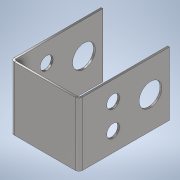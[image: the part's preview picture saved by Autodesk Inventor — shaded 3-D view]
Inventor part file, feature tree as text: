
AUTODESK INVENTOR PART (.ipt)
format: ipt  version: 2022 (Build 260153000, 153)  size: 192,512 bytes
history: native  units: mm
features: sheet_metal_op x3, sketch x2, other x2, extrude x1, projected_geometry x1
ambient origin geometry x8: Origin, YZ Plane, XZ Plane, XY Plane, X Axis, Y Axis, Z Axis, Center Point
bodies: Solid1 (feature_tree)
feature tree (9):
  sheet_metal_op  "Contour Flange1"
  extrude  "Extrusion1"  Depth=70.0mm
  sketch  "Sketch1"  dims[d0=51.0mm d1=70.0mm]
  other  "Plate1"
  sheet_metal_op  "Bend1"
  sheet_metal_op  "Corner1"
  sketch  "Sketch2"  dims[d2=70.0mm d3=1.5mm d4=1.5mm d5=0.75mm d6=3.0mm d7=1.5mm d8=50.0mm d9=1.5mm d10=1.5mm d11=6.0mm d12=1.5mm d13=1.5mm d20=18.0mm d21=15.0mm d22=25.0mm d23=0.0mm d24=0.0mm d29=10.2mm d30=10.2mm d31=27.0mm d32=27.0mm d33=20.0mm d34=15.0mm d35=50.0mm]
  projected_geometry  "Projected Loop1"
  other  "Definition1"
